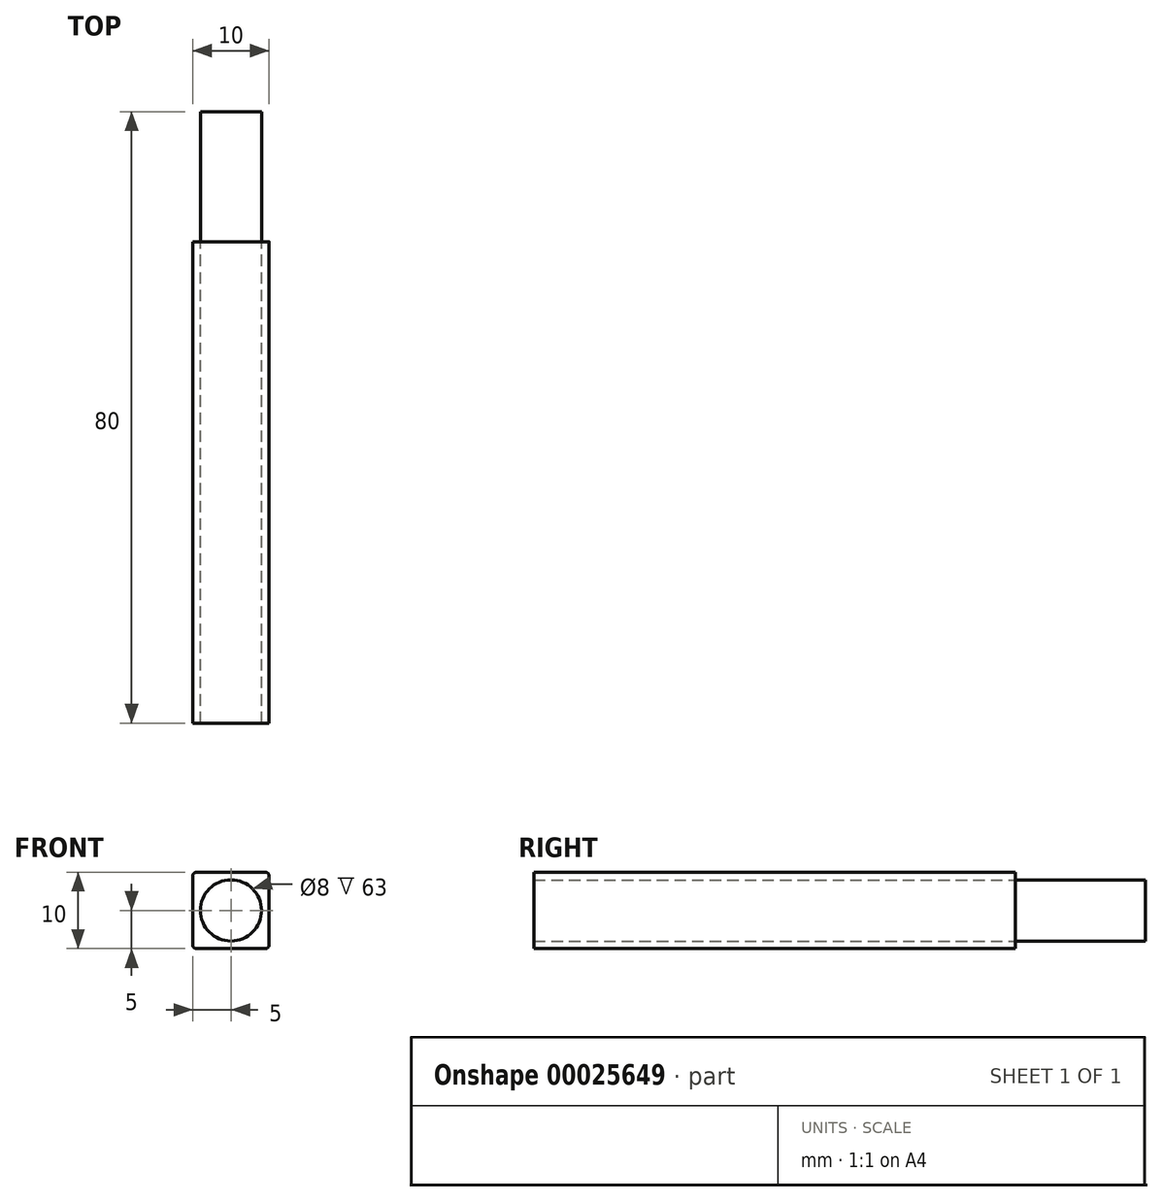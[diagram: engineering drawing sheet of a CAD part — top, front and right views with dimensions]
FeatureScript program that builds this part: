
annotation { "Feature Type Name" : "Feature", "Feature Type Description" : "" }
export const myFeature = defineFeature(function(context is Context, id is Id, definition is map)
    precondition{}
    {
        {
            var Q0;
            Q0=qCreatedBy(makeId("Front.planeOp"),FACE);
            var sketch = newSketch(context, id + "F0", { "sketchPlane" : qUnion([Q0])});
            skLineSegment(sketch, "E0.rect.bottom", {"start": v(4.5, -5) * mm, "end": v(-4.5, -5) * mm});
            skLineSegment(sketch, "E0.rect.top", {"start": v(4.5, 5) * mm, "end": v(-4.5, 5) * mm});
            skLineSegment(sketch, "E0.rect.left", {"start": v(5, -4.5) * mm, "end": v(5, 4.5) * mm});
            skLineSegment(sketch, "E0.rect.right", {"start": v(-5, -4.5) * mm, "end": v(-5, 4.5) * mm});
            skPoint(sketch, "E0.rect.middle", {"position": v(0, 0) * mm});
            skCircle(sketch, "E1", {"center": v(0, 0) * mm, "radius": 4 * mm});
            skPoint(sketch, "E2.visualSharp", {"position": v(-5, 5) * mm});
            skArc(sketch, "E2.filletArc", {"start": v(-4.5, 5) * mm, "mid": v(-4.85, 4.85) * mm, "end": v(-5, 4.5) * mm});
            skPoint(sketch, "E3.visualSharp", {"position": v(5, 5) * mm});
            skArc(sketch, "E3.filletArc", {"start": v(5, 4.5) * mm, "mid": v(4.85, 4.85) * mm, "end": v(4.5, 5) * mm});
            skPoint(sketch, "E4.visualSharp", {"position": v(5, -5) * mm});
            skArc(sketch, "E4.filletArc", {"start": v(4.5, -5) * mm, "mid": v(4.85, -4.85) * mm, "end": v(5, -4.5) * mm});
            skPoint(sketch, "E5.visualSharp", {"position": v(-5, -5) * mm});
            skArc(sketch, "E5.filletArc", {"start": v(-5, -4.5) * mm, "mid": v(-4.85, -4.85) * mm, "end": v(-4.5, -5) * mm});
            skSolve(sketch);
        }
        {
            var Q0;
            Q0=makeQuery(id+"F0.imprint","IMPRINT",FACE,{"disambiguationData":[TD([[makeQuery(id+"F0.imprint","IMPRINT",EDGE,{"derivedFrom":sQuery(id+"F0.wireOp",EDGE,"E0.rect.bottom")}),-1.0]])]});
            extrude(context, id + "F1", {"entities" : qUnion([Q0]), "depth" : 63 * mm});
        }
        {
            var Q0;
            Q0=qCreatedBy(makeId("Front.planeOp"),FACE);
            var sketch = newSketch(context, id + "F2", { "sketchPlane" : qUnion([Q0])});
            skCircle(sketch, "E6", {"center": v(0, 0) * mm, "radius": 4 * mm});
            skSolve(sketch);
        }
        {
            var Q0;
            Q0=qSketchRegion(id+"F2",true);
            extrude(context, id + "F3", {"entities" : qUnion([Q0]), "operationType" : NewBodyOperationType.ADD, "oppositeDirection" : true, "depth" : 17 * mm});
        }
    });
